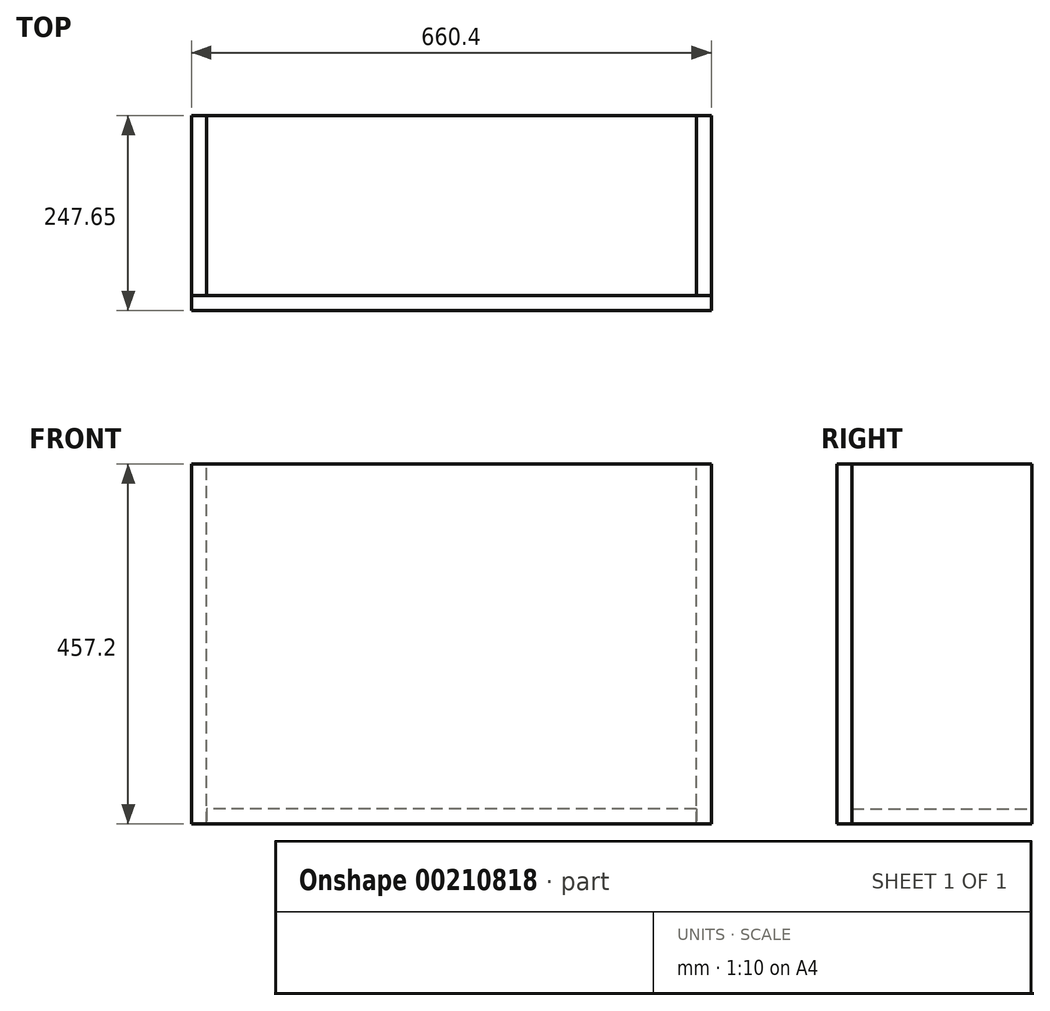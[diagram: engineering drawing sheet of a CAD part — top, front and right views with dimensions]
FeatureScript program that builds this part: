
annotation { "Feature Type Name" : "Feature", "Feature Type Description" : "" }
export const myFeature = defineFeature(function(context is Context, id is Id, definition is map)
    precondition{}
    {
        {
            var Q0;
            Q0=qCreatedBy(makeId("Front.planeOp"),FACE);
            var sketch = newSketch(context, id + "F0", { "sketchPlane" : qUnion([Q0])});
            skLineSegment(sketch, "E0.bottom", {"start": v(0, 0) * mm, "end": v(660.4, 0) * mm});
            skLineSegment(sketch, "E0.top", {"start": v(0, 457.2) * mm, "end": v(660.4, 457.2) * mm});
            skLineSegment(sketch, "E0.left", {"start": v(0, 0) * mm, "end": v(0, 457.2) * mm});
            skLineSegment(sketch, "E0.right", {"start": v(660.4, 0) * mm, "end": v(660.4, 457.2) * mm});
            skSolve(sketch);
        }
        {
            var Q0;
            Q0 = qSketchRegion(id + "F0", true);
            extrude(context, id + "F1", {"entities" : qUnion([Q0]), "depth" : 19.05 * mm, "offsetDistance" : 25.4 * mm});
        }
        {
            var Q0;
            Q0=makeQuery(id+"F1.opExtrude","SWEPT_FACE",FACE,{"disambiguationData":[OSD([sQuery(id+"F0.wireOp",EDGE,"E0.right")])]});
            var sketch = newSketch(context, id + "F2", { "sketchPlane" : qUnion([Q0])});
            skLineSegment(sketch, "E1.bottom", {"start": v(0, 0) * mm, "end": v(228.6, 0) * mm});
            skLineSegment(sketch, "E1.top", {"start": v(0, 457.2) * mm, "end": v(228.6, 457.2) * mm});
            skLineSegment(sketch, "E1.left", {"start": v(0, 0) * mm, "end": v(0, 457.2) * mm});
            skLineSegment(sketch, "E1.right", {"start": v(228.6, 0) * mm, "end": v(228.6, 457.2) * mm});
            skSolve(sketch);
        }
        {
            var Q0;
            Q0 = qSketchRegion(id + "F2", true);
            extrude(context, id + "F3", {"entities" : qUnion([Q0]), "oppositeDirection" : true, "depth" : 19.05 * mm, "offsetDistance" : 25.4 * mm});
        }
        {
            var Q0;
            Q0=makeQuery(id+"F1.opExtrude","SWEPT_FACE",FACE,{"disambiguationData":[OSD([sQuery(id+"F0.wireOp",EDGE,"E0.left")])]});
            var sketch = newSketch(context, id + "F4", { "sketchPlane" : qUnion([Q0])});
            skLineSegment(sketch, "E2.bottom", {"start": v(0, 0) * mm, "end": v(-228.6, 0) * mm});
            skLineSegment(sketch, "E2.top", {"start": v(0, 457.2) * mm, "end": v(-228.6, 457.2) * mm});
            skLineSegment(sketch, "E2.left", {"start": v(0, 0) * mm, "end": v(0, 457.2) * mm});
            skLineSegment(sketch, "E2.right", {"start": v(-228.6, 0) * mm, "end": v(-228.6, 457.2) * mm});
            skSolve(sketch);
        }
        {
            var Q0;
            Q0 = qSketchRegion(id + "F4", true);
            extrude(context, id + "F5", {"entities" : qUnion([Q0]), "oppositeDirection" : true, "depth" : 19.05 * mm, "offsetDistance" : 25.4 * mm});
        }
        {
            var Q0;
            Q0=makeQuery(id+"F3.opExtrude","SWEPT_FACE",FACE,{"disambiguationData":[OSD([sQuery(id+"F2.wireOp",EDGE,"E1.bottom")])]});
            var sketch = newSketch(context, id + "F6", { "sketchPlane" : qUnion([Q0])});
            skLineSegment(sketch, "E3.bottom", {"start": v(641.35, -228.6) * mm, "end": v(19.05, -228.6) * mm});
            skLineSegment(sketch, "E3.top", {"start": v(641.35, 0) * mm, "end": v(19.05, 0) * mm});
            skLineSegment(sketch, "E3.left", {"start": v(641.35, -228.6) * mm, "end": v(641.35, 0) * mm});
            skLineSegment(sketch, "E3.right", {"start": v(19.05, -228.6) * mm, "end": v(19.05, 0) * mm});
            skSolve(sketch);
        }
        {
            var Q0;
            Q0 = qSketchRegion(id + "F6", true);
            extrude(context, id + "F7", {"entities" : qUnion([Q0]), "oppositeDirection" : true, "depth" : 19.05 * mm, "offsetDistance" : 25.4 * mm});
        }
    });
